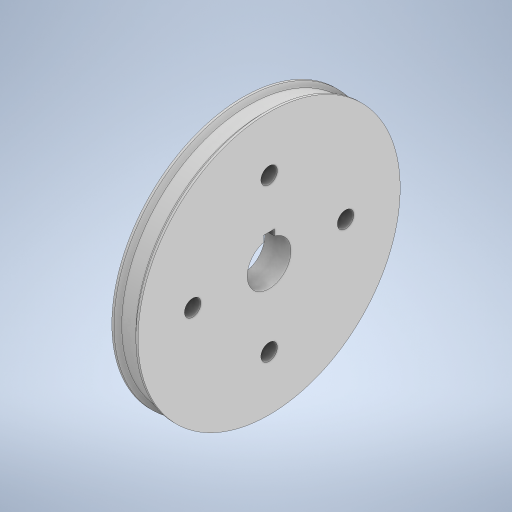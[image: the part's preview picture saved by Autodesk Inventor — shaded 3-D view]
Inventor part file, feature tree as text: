
AUTODESK INVENTOR PART (.ipt)
format: ipt  version: 2024 (Build 280153000, 153)  size: 271,872 bytes
history: native  units: mm
features: sketch x3, extrude x2, thicken_offset x2, revolve x1
ambient origin geometry x8: Origin, YZ Plane, XZ Plane, XY Plane, X Axis, Y Axis, Z Axis, Center Point
bodies: Solid1 (feature_tree)
feature tree (8):
  revolve  "Revolution1"  Angle=360.0deg
  extrude  "Extrusion1"  Depth=10.0mm
  thicken_offset  "Thicken1"
  thicken_offset  "Thicken2"
  extrude  "Extrusion2"  Depth=10.0mm
  sketch  "Sketch1"  dims[d3=90.0deg d6=40.0mm d8=360.0deg]
  sketch  "Sketch2"  dims[d10=100.0mm d11=0.0mm d12=10.0mm]
  sketch  "Sketch3"  dims[d13=10.0mm d14=10.0mm d15=10.0mm d18=120.0mm d19=0.0mm d20=0.5mm d21=0.872665mm]
